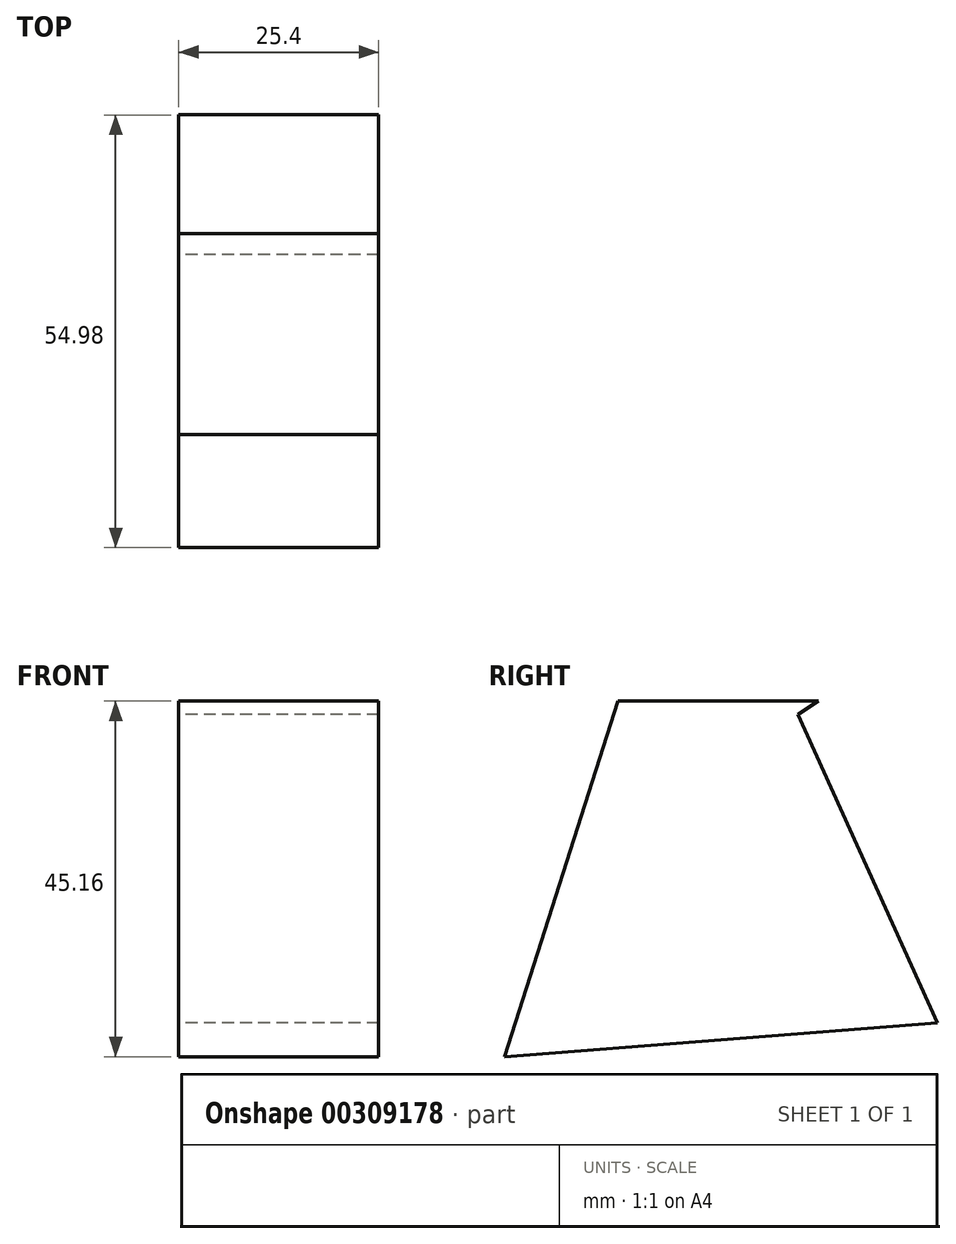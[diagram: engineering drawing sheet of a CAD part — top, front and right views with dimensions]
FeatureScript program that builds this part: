
annotation { "Feature Type Name" : "Feature", "Feature Type Description" : "" }
export const myFeature = defineFeature(function(context is Context, id is Id, definition is map)
    precondition{}
    {
        {
            var Q0;
            Q0=qCreatedBy(makeId("Right.planeOp"),FACE);
            var sketch = newSketch(context, id + "F0", { "sketchPlane" : qUnion([Q0])});
            skLineSegment(sketch, "E0", {"start": v(0, 0) * mm, "end": v(-39.6, 0) * mm});
            skLineSegment(sketch, "E1", {"start": v(-39.6, 0) * mm, "end": v(-54, -45.16) * mm});
            skLineSegment(sketch, "E2", {"start": v(-54, -45.16) * mm, "end": v(0.98, -40.87) * mm});
            skLineSegment(sketch, "E3", {"start": v(0.98, -40.87) * mm, "end": v(-16.75, -1.66) * mm});
            skLineSegment(sketch, "E4", {"start": v(-16.75, -1.66) * mm, "end": v(0.02, 8.97) * mm});
            skLineSegment(sketch, "E5", {"start": v(0.02, 8.97) * mm, "end": v(-12.9, 0.23) * mm});
            skSolve(sketch);
        }
        {
            var Q0;
            Q0 = qSketchRegion(id + "F0", true);
            extrude(context, id + "F1", {"entities" : qUnion([Q0]), "depth" : 25.4 * mm});
        }
    });
